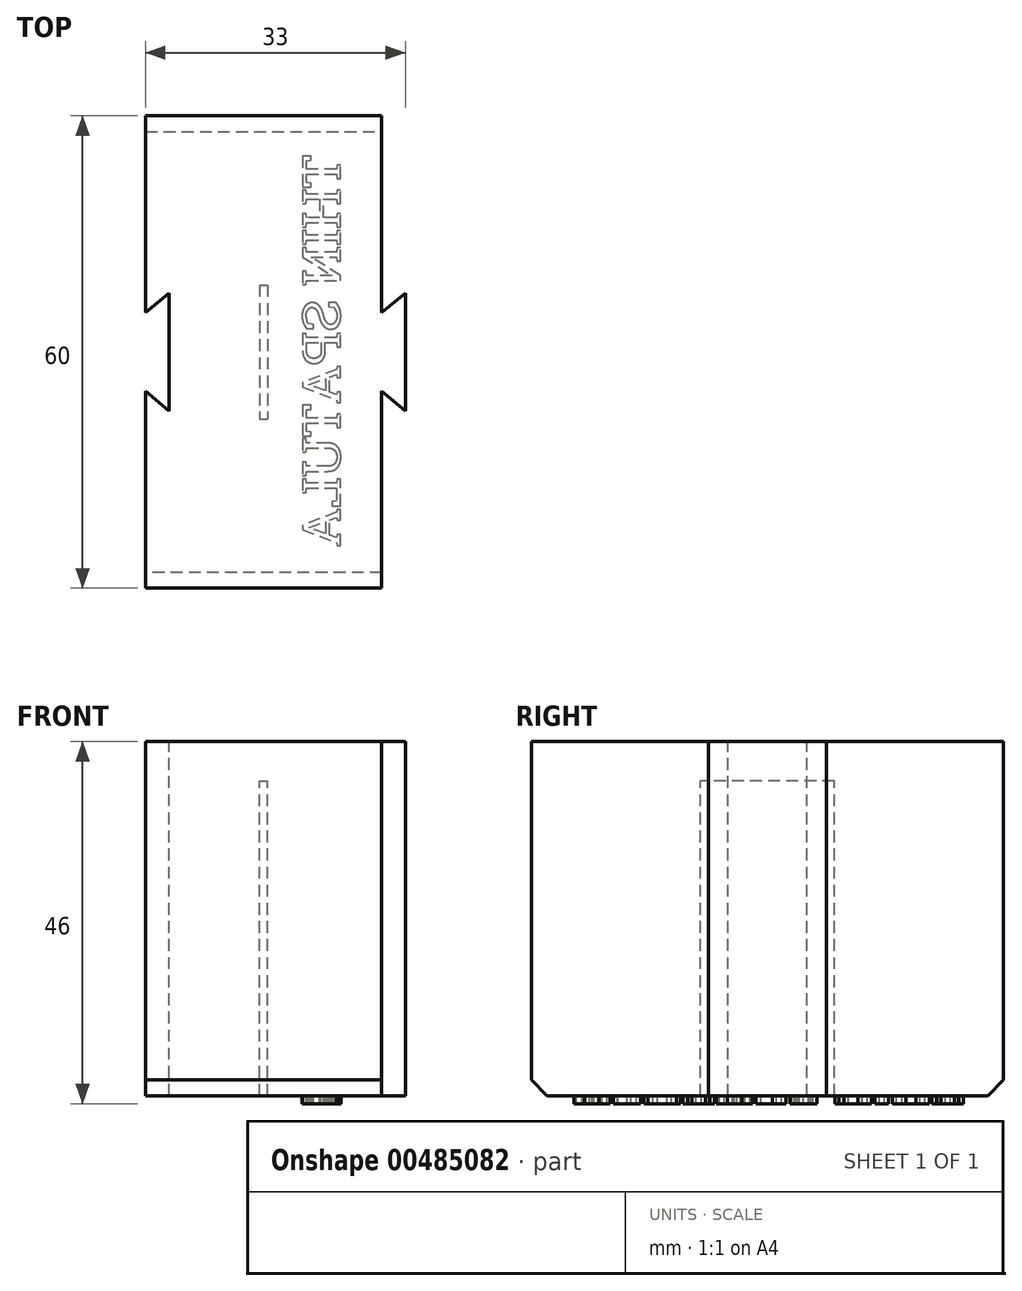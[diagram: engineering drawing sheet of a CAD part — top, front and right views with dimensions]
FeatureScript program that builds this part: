
annotation { "Feature Type Name" : "Feature", "Feature Type Description" : "" }
export const myFeature = defineFeature(function(context is Context, id is Id, definition is map)
    precondition{}
    {
        {
            var Q0;
            Q0=qCreatedBy(makeId("Top.planeOp"),FACE);
            var sketch = newSketch(context, id + "F0", { "sketchPlane" : qUnion([Q0])});
            skPoint(sketch, "E0.middle", {"position": v(0, 0) * mm});
            skLineSegment(sketch, "E1.bottom", {"start": v(15, 30) * mm, "end": v(-15, 30) * mm});
            skLineSegment(sketch, "E1.top", {"start": v(15, -30) * mm, "end": v(-15, -30) * mm});
            skLineSegment(sketch, "E2.left", {"start": v(-12, 7.5) * mm, "end": v(-12, -7.5) * mm});
            skLineSegment(sketch, "E3.left", {"start": v(18, 7.5) * mm, "end": v(18, -7.5) * mm});
            skLineSegment(sketch, "E4", {"start": v(-12, 7.5) * mm, "end": v(-15, 5) * mm});
            skLineSegment(sketch, "E5", {"start": v(15, 30) * mm, "end": v(15, 5) * mm});
            skLineSegment(sketch, "E6", {"start": v(15, -5) * mm, "end": v(15, -30) * mm});
            skLineSegment(sketch, "E7", {"start": v(-15, -30) * mm, "end": v(-15, -5) * mm});
            skLineSegment(sketch, "E8", {"start": v(-12, -7.5) * mm, "end": v(-12, 7.5) * mm});
            skLineSegment(sketch, "E9", {"start": v(-15, -5) * mm, "end": v(-12, -7.5) * mm});
            skLineSegment(sketch, "E10", {"start": v(-15, 5) * mm, "end": v(-15, 30) * mm});
            skLineSegment(sketch, "E11", {"start": v(15, 5) * mm, "end": v(18, 7.5) * mm});
            skLineSegment(sketch, "E12", {"start": v(15, -5) * mm, "end": v(18, -7.5) * mm});
            skLineSegment(sketch, "E13.bottom", {"start": v(-0.5, 8.5) * mm, "end": v(0.5, 8.5) * mm});
            skLineSegment(sketch, "E13.top", {"start": v(-0.5, -8.5) * mm, "end": v(0.5, -8.5) * mm});
            skLineSegment(sketch, "E13.left", {"start": v(-0.5, 8.5) * mm, "end": v(-0.5, -8.5) * mm});
            skLineSegment(sketch, "E13.right", {"start": v(0.5, 8.5) * mm, "end": v(0.5, -8.5) * mm});
            skSolve(sketch);
        }
        {
            var Q0;
            Q0=makeQuery(id+"F0.imprint","IMPRINT",FACE,{"disambiguationData":[TD([[makeQuery(id+"F0.imprint","IMPRINT",EDGE,{"derivedFrom":sQuery(id+"F0.wireOp",EDGE,"E1.bottom")}),1.0]])]});
            extrude(context, id + "F1", {"entities" : qUnion([Q0]), "oppositeDirection" : true, "depth" : 40 * mm});
        }
        {
            var Q0;
            Q0=makeQuery(id+"F0.imprint","IMPRINT",FACE,{"disambiguationData":[TD([[makeQuery(id+"F0.imprint","IMPRINT",EDGE,{"derivedFrom":sQuery(id+"F0.wireOp",EDGE,"E13.bottom")}),-1.0]])]});
            var Q1;
            Q1=makeQuery(id+"F0.imprint","IMPRINT",FACE,{"disambiguationData":[TD([[makeQuery(id+"F0.imprint","IMPRINT",EDGE,{"derivedFrom":sQuery(id+"F0.wireOp",EDGE,"E1.bottom")}),1.0]])]});
            extrude(context, id + "F2", {"entities" : qUnion([Q0, Q1]), "operationType" : NewBodyOperationType.ADD, "depth" : 5 * mm});
        }
        {
            var Q0;
            Q0=makeQuery(id+"F1.opExtrude","CAP_FACE",FACE,{"disambiguationData":[OSD([sQuery(id+"F0.wireOp",EDGE,"E1.bottom"),sQuery(id+"F0.wireOp",EDGE,"E1.top"),sQuery(id+"F0.wireOp",EDGE,"E4"),sQuery(id+"F0.wireOp",EDGE,"E5"),sQuery(id+"F0.wireOp",EDGE,"E3.left"),sQuery(id+"F0.wireOp",EDGE,"E6"),sQuery(id+"F0.wireOp",EDGE,"E7"),sQuery(id+"F0.wireOp",EDGE,"E8"),sQuery(id+"F0.wireOp",EDGE,"E9"),sQuery(id+"F0.wireOp",EDGE,"E10"),sQuery(id+"F0.wireOp",EDGE,"E11"),sQuery(id+"F0.wireOp",EDGE,"E12"),sQuery(id+"F0.wireOp",EDGE,"E13.bottom"),sQuery(id+"F0.wireOp",EDGE,"E13.top"),sQuery(id+"F0.wireOp",EDGE,"E13.left"),sQuery(id+"F0.wireOp",EDGE,"E13.right")])],"isStart":false});
            var sketch = newSketch(context, id + "F3", { "sketchPlane" : qUnion([Q0])});
            skText(sketch, "E14", { "text": "THIN SPATULA", "fontName": "RobotoSlab-Regular.ttf"});
            const initialGuessF3  = {"E14": [0.00974, -0.02501, 0, 1, 0.00484]};
            skSetInitialGuess(sketch, initialGuessF3);
            skSolve(sketch);
        }
        {
            var Q0;
            Q0 = qSketchRegion(id + "F3", true);
            extrude(context, id + "F4", {"entities" : qUnion([Q0]), "operationType" : NewBodyOperationType.ADD, "depth" : 1 * mm});
        }
        {
            var Q0;
            Q0=makeQuery(id+"F1.opExtrude","CAP_EDGE",EDGE,{"disambiguationData":[OSD([sQuery(id+"F0.wireOp",EDGE,"E1.bottom")])],"isStart":false});
            var Q1;
            Q1=makeQuery(id+"F1.opExtrude","CAP_EDGE",EDGE,{"disambiguationData":[OSD([sQuery(id+"F0.wireOp",EDGE,"E1.top")])],"isStart":false});
            chamfer(context, id + "F5", {"entities" : qUnion([Q0, Q1]), "width" : 2 * mm, "tangentPropagation" : true});
        }
    });
